# Revit family: 00-7986-05-M1
name_source: partatom
category: Luminarias
revit_build: Autodesk Revit 2017 (Build: 20160225_1515(x64)
units: mm (PartAtom-declared; Revit-internal decimal feet)

## family parameters
Anfitrión = Cara
Compartido = Sí
Corte con vacíos al cargar = No
Cota de conector redondo = Diámetro de uso
Número OmniClass = 23.80.70.00
Origen de luz = No
Punto de cálculo de habitación = No
Tipo de pieza = Normal
Título OmniClass = Lighting

## types (1)
- 00-7986-05-M1
    Acabado = Negro, Blanco
    CRI = 0
    Carga aparente = 0 VA
    Catálogo = Decorative
    CodigoGubimclass = 50.60.50.20
    CodigoOmniclass = 21-04 50 40
    CodigoUniclass2015 = EF_70_80
    CodigoUniformat2010 = D5040
    DescripcionGubimclass = Iluminación interior
    DescripcionOmniclass = Lighting
    DescripcionUniclass2015 = Lighting
    DescripcionUniformat2010 = Lighting
    EAN13 = 8435575369757
    Eficiencia energética = NO BULB
    Elevación por defecto = 1000 mm  [stored 3.28084 ft]
    Etiqueta V/f = 100-240V/50-60Hz
    Fabricante = LEDS C4
    Familia = Coco Chandelier
    FechaVersion = Julio 2020
    Ficha = http://files.leds-c4.com
    IMC = http://files.leds-c4.com
    IP = IP20
    IfcExportAs = IfcLightFixture
IfcLightFixture
    IfcExportType = NOTDEFINED
    Imagen web = http://files.leds-c4.com
    Lumenes reales (lm) = 0
    Material = Acero, Aluminio, Policarbonato
    Peso neto (KG) = 0
    Producto descatalogado = Catalogado ES
    Referencia = 00-7986-05-M1
    Tender text (Castellano) = LEDS C4
Coco Chandelier
00-7986-05-M1

de uso interior 
Material estructura: Acero, Aluminio. Acabado estructura: Negro. Material difusor: Policarbonato. Acabado difusor: Blanco. Garantía: 5 Años.

Peso neto del producto (Kg): 0.000
Anchura o diámetro del producto (mm): 1300
Altura del producto (mm): 2300

Clase 1. IP: IP20. E14. Nº de portalámparas o Leds: 6. Potencia máxima de la fuente de luz: 7W. Equipo incluido: No. Potencia total: 42.
    Tender text (English) = LEDS C4
Coco Chandelier
00-7986-05-M1

for indoor use. 
Structure material: Steel, Aluminium. Structure finish: Black. Diffuser material: Polycarbonate. Diffuser finish: White. Warranty: 5 Years.

Product net weight (Kg): 0.000
Product width or diameter (mm): 1300
Product height (mm): 2300

Class 1. IP: IP20. E14. No. of lampholders or LEDs: 6. Maximum power of light source: 7W. Gear included: No. Total power: 42.
    Tipo = Colgante
    Vatios (W) = 42
    Versión = v1

note: [stored X ft] marks values corroborated as IEEE doubles in the binary element streams (Revit-internal decimal feet)
